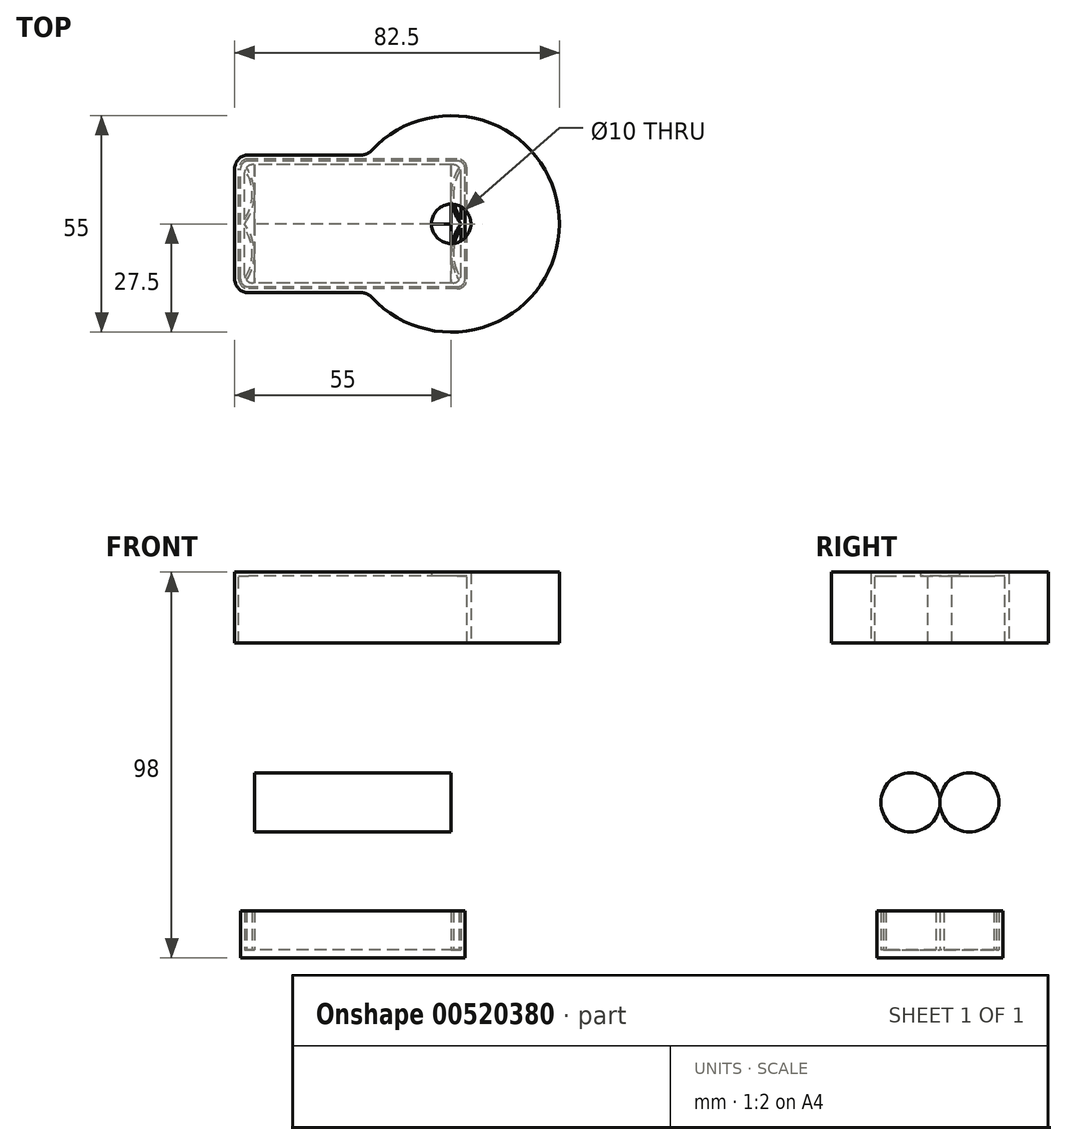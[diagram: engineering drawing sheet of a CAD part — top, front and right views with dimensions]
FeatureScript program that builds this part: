
annotation { "Feature Type Name" : "Feature", "Feature Type Description" : "" }
export const myFeature = defineFeature(function(context is Context, id is Id, definition is map)
    precondition{}
    {
        {
            var Q0;
            Q0=qCreatedBy(makeId("Top.planeOp"),FACE);
            var sketch = newSketch(context, id + "F0", { "sketchPlane" : qUnion([Q0])});
            skLineSegment(sketch, "E0.bottom", {"start": v(28.5, -16) * mm, "end": v(-28.5, -16) * mm});
            skLineSegment(sketch, "E0.top", {"start": v(28.5, 16) * mm, "end": v(-28.5, 16) * mm});
            skLineSegment(sketch, "E0.left", {"start": v(28.5, -16) * mm, "end": v(28.5, 16) * mm});
            skLineSegment(sketch, "E0.right", {"start": v(-28.5, -16) * mm, "end": v(-28.5, 16) * mm});
            skPoint(sketch, "E0.middle", {"position": v(0, 0) * mm});
            skLineSegment(sketch, "E1.bottom", {"start": v(27.5, -15) * mm, "end": v(-27.5, -15) * mm});
            skLineSegment(sketch, "E1.top", {"start": v(27.5, 15) * mm, "end": v(-27.5, 15) * mm});
            skLineSegment(sketch, "E1.left", {"start": v(27.5, -15) * mm, "end": v(27.5, 15) * mm});
            skLineSegment(sketch, "E1.right", {"start": v(-27.5, -15) * mm, "end": v(-27.5, 15) * mm});
            skSolve(sketch);
        }
        {
            var Q0;
            Q0=makeQuery(id+"F0.imprint","IMPRINT",FACE,{"disambiguationData":[TD([[makeQuery(id+"F0.imprint","IMPRINT",EDGE,{"derivedFrom":sQuery(id+"F0.wireOp",EDGE,"E0.bottom")}),-1.0]])]});
            var Q1;
            Q1=makeQuery(id+"F0.imprint","IMPRINT",FACE,{"disambiguationData":[TD([[makeQuery(id+"F0.imprint","IMPRINT",EDGE,{"derivedFrom":sQuery(id+"F0.wireOp",EDGE,"E1.bottom")}),-1.0]])]});
            extrude(context, id + "F1", {"entities" : qUnion([Q0, Q1]), "oppositeDirection" : true, "depth" : 2 * mm});
        }
        {
            var Q0;
            Q0=makeQuery(id+"F0.imprint","IMPRINT",FACE,{"disambiguationData":[TD([[makeQuery(id+"F0.imprint","IMPRINT",EDGE,{"derivedFrom":sQuery(id+"F0.wireOp",EDGE,"511JZqgd-saJz-wMDc-ROUc-2f22ZJkLcz4P.bottom")}),-1.0]])]});
            var Q1;
            {var subQ0=sQuery(id+"F0.wireOp",EDGE,"E0.bottom");Q1=makeQuery(id+"F0.imprint","IMPRINT",FACE,{"disambiguationData":[TD([[makeQuery(id+"F0.imprint","IMPRINT",EDGE,{"derivedFrom":subQ0}),-1.0]])]});}
            extrude(context, id + "F2", {"entities" : qUnion([Q0, Q1]), "operationType" : NewBodyOperationType.ADD, "depth" : 10 * mm});
        }
        {
            var Q0;
            Q0=makeQuery(id+"F2.opExtrude","SWEPT_EDGE",EDGE,{"disambiguationData":[OSD([sQuery(id+"F0.wireOp",EDGE,"E1.top"),sQuery(id+"F0.wireOp",EDGE,"E1.right")])]});
            var Q1;
            {var subQ0=sQuery(id+"F0.wireOp",EDGE,"E0.right");var subQ1=sQuery(id+"F0.wireOp",EDGE,"E0.top");Q1=makeQuery(id+"F2.boolean.opBoolean","MERGE",EDGE,{"derivedFrom":[makeQuery(id+"F1.opExtrude","SWEPT_EDGE",EDGE,{"disambiguationData":[OSD([subQ1,subQ0])]}),makeQuery(id+"F2.opExtrude","SWEPT_EDGE",EDGE,{"disambiguationData":[OSD([subQ1,subQ0])]})]});}
            var Q2;
            Q2=makeQuery(id+"F2.opExtrude","SWEPT_EDGE",EDGE,{"disambiguationData":[OSD([sQuery(id+"F0.wireOp",EDGE,"E1.bottom"),sQuery(id+"F0.wireOp",EDGE,"E1.right")])]});
            var Q3;
            {var subQ0=sQuery(id+"F0.wireOp",EDGE,"E0.left");var subQ1=sQuery(id+"F0.wireOp",EDGE,"E0.top");Q3=makeQuery(id+"F2.boolean.opBoolean","MERGE",EDGE,{"derivedFrom":[makeQuery(id+"F1.opExtrude","SWEPT_EDGE",EDGE,{"disambiguationData":[OSD([subQ1,subQ0])]}),makeQuery(id+"F2.opExtrude","SWEPT_EDGE",EDGE,{"disambiguationData":[OSD([subQ1,subQ0])]})]});}
            var Q4;
            {var subQ0=sQuery(id+"F0.wireOp",EDGE,"E0.right");var subQ1=sQuery(id+"F0.wireOp",EDGE,"E0.bottom");Q4=makeQuery(id+"F2.boolean.opBoolean","MERGE",EDGE,{"derivedFrom":[makeQuery(id+"F1.opExtrude","SWEPT_EDGE",EDGE,{"disambiguationData":[OSD([subQ1,subQ0])]}),makeQuery(id+"F2.opExtrude","SWEPT_EDGE",EDGE,{"disambiguationData":[OSD([subQ1,subQ0])]})]});}
            var Q5;
            Q5=makeQuery(id+"F2.opExtrude","SWEPT_EDGE",EDGE,{"disambiguationData":[OSD([sQuery(id+"F0.wireOp",EDGE,"E1.top"),sQuery(id+"F0.wireOp",EDGE,"E1.left")])]});
            var Q6;
            Q6=makeQuery(id+"F2.opExtrude","SWEPT_EDGE",EDGE,{"disambiguationData":[OSD([sQuery(id+"F0.wireOp",EDGE,"E1.bottom"),sQuery(id+"F0.wireOp",EDGE,"E1.left")])]});
            var Q7;
            {var subQ0=sQuery(id+"F0.wireOp",EDGE,"E0.left");var subQ1=sQuery(id+"F0.wireOp",EDGE,"E0.bottom");Q7=makeQuery(id+"F2.boolean.opBoolean","MERGE",EDGE,{"derivedFrom":[makeQuery(id+"F1.opExtrude","SWEPT_EDGE",EDGE,{"disambiguationData":[OSD([subQ1,subQ0])]}),makeQuery(id+"F2.opExtrude","SWEPT_EDGE",EDGE,{"disambiguationData":[OSD([subQ1,subQ0])]})]});}
            var Q8;
            Q8=makeQuery(id+"F2.opExtrude","CAP_EDGE",EDGE,{"disambiguationData":[OSD([sQuery(id+"F0.wireOp",EDGE,"E1.top")])],"isStart":true});
            var Q9;
            Q9=makeQuery(id+"F2.opExtrude","CAP_EDGE",EDGE,{"disambiguationData":[OSD([sQuery(id+"F0.wireOp",EDGE,"E1.bottom")])],"isStart":true});
            fillet(context, id + "F3", {"entities" : qUnion([Q0, Q1, Q2, Q3, Q4, Q5, Q6, Q7, Q8, Q9]), "radius" : 2 * mm, "tangentPropagation" : true, "allowEdgeOverflow" : false});
        }
        {
            var Q0;
            Q0=qCreatedBy(makeId("Right.planeOp"),FACE);
            var sketch = newSketch(context, id + "F4", { "sketchPlane" : qUnion([Q0])});
            skCircle(sketch, "E2", {"center": v(-7.5, 7.5) * mm, "radius": 7.5 * mm});
            skCircle(sketch, "E3.MirrorC", {"center": v(7.5, 7.5) * mm, "radius": 7.5 * mm});
            skSolve(sketch);
        }
        {
            var Q0;
            Q0=qSketchRegion(id+"F4",true);
            extrude(context, id + "F5", {"entities" : qUnion([Q0]), "endBound" : BoundingType.SYMMETRIC, "depth" : 50 * mm});
        }
        {
            var Q0;
            Q0=qCreatedBy(makeId("Top.planeOp"),FACE);
            var sketch = newSketch(context, id + "F6", { "sketchPlane" : qUnion([Q0])});
            skLineSegment(sketch, "E4.0", {"start": v(-27.5, -15) * mm, "end": v(-27.5, 15) * mm, "construction": true});
            skLineSegment(sketch, "E5.0", {"start": v(-25, 0) * mm, "end": v(-25, 15) * mm, "construction": true});
            skArc(sketch, "E6", {"start": v(-27.5, 0) * mm, "mid": v(-25, 7.5) * mm, "end": v(-27.5, 15) * mm});
            skArc(sketch, "E7", {"start": v(-27.5, 1.05) * mm, "mid": v(-25.6, 7.5) * mm, "end": v(-27.5, 13.95) * mm});
            skLineSegment(sketch, "E8", {"start": v(-27.5, 15) * mm, "end": v(-27.5, 13.95) * mm});
            skLineSegment(sketch, "E9", {"start": v(-27.5, 1.05) * mm, "end": v(-27.5, 0) * mm});
            skLineSegment(sketch, "E10.MirrorCS", {"start": v(-27.5, -15) * mm, "end": v(-27.5, -13.95) * mm});
            skArc(sketch, "E11.MirrorCS", {"start": v(-27.5, -1.05) * mm, "mid": v(-25.6, -7.5) * mm, "end": v(-27.5, -13.95) * mm});
            skArc(sketch, "E12.MirrorCS", {"start": v(-27.5, 0) * mm, "mid": v(-25, -7.5) * mm, "end": v(-27.5, -15) * mm});
            skLineSegment(sketch, "E13.MirrorCS", {"start": v(-27.5, -1.05) * mm, "end": v(-27.5, 0) * mm});
            skLineSegment(sketch, "E14.MirrorCS", {"start": v(-25, 0) * mm, "end": v(-25, -15) * mm, "construction": true});
            skLineSegment(sketch, "E15.MirrorCS", {"start": v(27.5, -1.05) * mm, "end": v(27.5, 0) * mm});
            skLineSegment(sketch, "E16.MirrorCS", {"start": v(27.5, -15) * mm, "end": v(27.5, -13.95) * mm});
            skLineSegment(sketch, "E17.MirrorCS", {"start": v(27.5, 15) * mm, "end": v(27.5, 13.95) * mm});
            skLineSegment(sketch, "E18.MirrorCS", {"start": v(27.5, 1.05) * mm, "end": v(27.5, 0) * mm});
            skLineSegment(sketch, "E19.MirrorCS", {"start": v(27.5, -15) * mm, "end": v(27.5, 15) * mm, "construction": true});
            skLineSegment(sketch, "E20.MirrorCS", {"start": v(25, 0) * mm, "end": v(25, -15) * mm, "construction": true});
            skArc(sketch, "E21.MirrorCS", {"start": v(27.5, 0) * mm, "mid": v(25, -7.5) * mm, "end": v(27.5, -15) * mm});
            skArc(sketch, "E22.MirrorCS", {"start": v(27.5, 0) * mm, "mid": v(25, 7.5) * mm, "end": v(27.5, 15) * mm});
            skLineSegment(sketch, "E23.MirrorCS", {"start": v(25, 0) * mm, "end": v(25, 15) * mm, "construction": true});
            skArc(sketch, "E24.MirrorCS", {"start": v(27.5, 1.05) * mm, "mid": v(25.6, 7.5) * mm, "end": v(27.5, 13.95) * mm});
            skArc(sketch, "E25.MirrorCS", {"start": v(27.5, -1.05) * mm, "mid": v(25.6, -7.5) * mm, "end": v(27.5, -13.95) * mm});
            skSolve(sketch);
        }
        {
            var Q0;
            Q0=makeQuery(id+"F6.imprint","IMPRINT",FACE,{"disambiguationData":[TD([[makeQuery(id+"F6.imprint","IMPRINT",EDGE,{"derivedFrom":sQuery(id+"F6.wireOp",EDGE,"E6")}),1.0]])]});
            var Q1;
            Q1=makeQuery(id+"F6.imprint","IMPRINT",FACE,{"disambiguationData":[TD([[makeQuery(id+"F6.imprint","IMPRINT",EDGE,{"derivedFrom":sQuery(id+"F6.wireOp",EDGE,"E10.MirrorCS")}),-1.0]])]});
            var Q2;
            Q2=makeQuery(id+"F6.imprint","IMPRINT",FACE,{"disambiguationData":[TD([[makeQuery(id+"F6.imprint","IMPRINT",EDGE,{"derivedFrom":sQuery(id+"F6.wireOp",EDGE,"E17.MirrorCS")}),-1.0]])]});
            var Q3;
            Q3=makeQuery(id+"F6.imprint","IMPRINT",FACE,{"disambiguationData":[TD([[makeQuery(id+"F6.imprint","IMPRINT",EDGE,{"derivedFrom":sQuery(id+"F6.wireOp",EDGE,"E15.MirrorCS")}),1.0]])]});
            extrude(context, id + "F7", {"entities" : qUnion([Q0, Q1, Q2, Q3]), "operationType" : NewBodyOperationType.ADD, "depth" : 10 * mm});
        }
        {
            var Q0;
            Q0=qCreatedBy(makeId("Top.planeOp"),FACE);
            cPlane(context, id + "F8", {"entities" : qUnion([Q0]), "cplaneType" : CPlaneType.OFFSET, "offset" : 15 * mm, "width" : 150 * mm, "height" : 150 * mm});
        }
        {
            var Q0;
            Q0=qCreatedBy(id+"F8.planeOp",FACE);
            var sketch = newSketch(context, id + "F9", { "sketchPlane" : qUnion([Q0])});
            skLineSegment(sketch, "E26.bottom", {"start": v(26.5, -16.5) * mm, "end": v(-26.5, -16.5) * mm});
            skLineSegment(sketch, "E26.top", {"start": v(26.5, 16.5) * mm, "end": v(-26.5, 16.5) * mm});
            skLineSegment(sketch, "E26.left", {"start": v(29, -14) * mm, "end": v(29, 14) * mm});
            skLineSegment(sketch, "E26.right", {"start": v(-29, -14) * mm, "end": v(-29, 14) * mm});
            skPoint(sketch, "E26.middle", {"position": v(0, 0) * mm});
            skPoint(sketch, "E27.visualSharp", {"position": v(-29, 16.5) * mm});
            skArc(sketch, "E27.filletArc", {"start": v(-26.5, 16.5) * mm, "mid": v(-28.27, 15.77) * mm, "end": v(-29, 14) * mm});
            skPoint(sketch, "E28.visualSharp", {"position": v(29, 16.5) * mm});
            skArc(sketch, "E28.filletArc", {"start": v(29, 14) * mm, "mid": v(28.27, 15.77) * mm, "end": v(26.5, 16.5) * mm});
            skPoint(sketch, "E29.visualSharp", {"position": v(29, -16.5) * mm});
            skArc(sketch, "E29.filletArc", {"start": v(26.5, -16.5) * mm, "mid": v(28.27, -15.77) * mm, "end": v(29, -14) * mm});
            skPoint(sketch, "E30.visualSharp", {"position": v(-29, -16.5) * mm});
            skArc(sketch, "E30.filletArc", {"start": v(-29, -14) * mm, "mid": v(-28.27, -15.77) * mm, "end": v(-26.5, -16.5) * mm});
            skLineSegment(sketch, "E31.bottom", {"start": v(2.2, -17.5) * mm, "end": v(-26.5, -17.5) * mm});
            skLineSegment(sketch, "E31.top", {"start": v(2.2, 17.5) * mm, "end": v(-26.5, 17.5) * mm});
            skLineSegment(sketch, "E31.left", {"start": v(30, -27.04) * mm, "end": v(30, 27.04) * mm});
            skLineSegment(sketch, "E31.right", {"start": v(-30, -14) * mm, "end": v(-30, 14) * mm});
            skPoint(sketch, "E32.visualSharp", {"position": v(-30, 17.5) * mm});
            skArc(sketch, "E32.filletArc", {"start": v(-26.5, 17.5) * mm, "mid": v(-28.97, 16.47) * mm, "end": v(-30, 14) * mm});
            skPoint(sketch, "E33.visualSharp", {"position": v(-30, -17.5) * mm});
            skArc(sketch, "E33.filletArc", {"start": v(-30, -14) * mm, "mid": v(-28.97, -16.47) * mm, "end": v(-26.5, -17.5) * mm});
            skArc(sketch, "E34", {"start": v(4.77, -18.63) * mm, "mid": v(52.5, 0) * mm, "end": v(4.77, 18.63) * mm});
            skPoint(sketch, "E35.orphan", {"position": v(30, 17.5) * mm});
            skPoint(sketch, "E36.orphan", {"position": v(30, -17.5) * mm});
            skCircle(sketch, "E37", {"center": v(25, 0) * mm, "radius": 5 * mm});
            skPoint(sketch, "E38.visualSharp", {"position": v(3.79, 17.5) * mm});
            skArc(sketch, "E38.filletArc", {"start": v(2.2, 17.5) * mm, "mid": v(3.6, 17.8) * mm, "end": v(4.77, 18.63) * mm});
            skPoint(sketch, "E39.visualSharp", {"position": v(3.79, -17.5) * mm});
            skArc(sketch, "E39.filletArc", {"start": v(4.77, -18.63) * mm, "mid": v(3.6, -17.8) * mm, "end": v(2.2, -17.5) * mm});
            skSolve(sketch);
        }
        {
            var Q0;
            Q0=makeQuery(id+"F9.imprint","IMPRINT",FACE,{"disambiguationData":[TD([[makeQuery(id+"F9.imprint","IMPRINT",EDGE,{"derivedFrom":sQuery(id+"F9.wireOp",EDGE,"E26.bottom")}),-1.0]])]});
            var Q1;
            Q1=makeQuery(id+"F9.imprint","IMPRINT",FACE,{"disambiguationData":[TD([[makeQuery(id+"F9.imprint","IMPRINT",EDGE,{"derivedFrom":sQuery(id+"F9.wireOp",EDGE,"E26.bottom")}),1.0]])]});
            var Q2;
            {var subQ0=sQuery(id+"F9.wireOp",EDGE,"E34");var subQ1=sQuery(id+"F9.wireOp",EDGE,"E31.left");var subQ2=makeQuery(id+"F9.imprint","INTERSECT",VERTEX,{"disambiguationData":[OD(0.0)],"derivedFrom":[subQ1,subQ0]});Q2=makeQuery(id+"F9.imprint","IMPRINT",FACE,{"disambiguationData":[TD([[makeQuery(id+"F9.imprint","IMPRINT",EDGE,{"disambiguationData":[TD([[subQ2,-1.0]])],"derivedFrom":subQ1}),-1.0]])]});}
            extrude(context, id + "F10", {"entities" : qUnion([Q0, Q1, Q2]), "depth" : 1 * mm});
        }
        {
            var Q0;
            Q0=qSketchRegion(id+"F9",true);
            var Q1;
            {var subQ0=sQuery(id+"F9.wireOp",EDGE,"E37");var subQ1=sQuery(id+"F9.wireOp",EDGE,"E26.left");var subQ2=makeQuery(id+"F9.imprint","INTERSECT",VERTEX,{"disambiguationData":[OD(0.0)],"derivedFrom":[subQ1,subQ0]});Q1=makeQuery(id+"F9.imprint","IMPRINT",FACE,{"disambiguationData":[TD([[makeQuery(id+"F9.imprint","IMPRINT",EDGE,{"disambiguationData":[TD([[subQ2,-1.0]])],"derivedFrom":subQ1}),-1.0]])]});}
            extrude(context, id + "F11", {"entities" : qUnion([Q0, Q1]), "operationType" : NewBodyOperationType.ADD, "oppositeDirection" : true, "depth" : 17 * mm});
        }
        {
            var Q0;
            Q0=makeQuery(id+"F10.opExtrude","SWEPT_BODY",BODY,{"disambiguationData":[OSD([sQuery(id+"F9.wireOp",EDGE,"E31.bottom"),sQuery(id+"F9.wireOp",EDGE,"E31.top"),sQuery(id+"F9.wireOp",EDGE,"E31.right"),sQuery(id+"F9.wireOp",EDGE,"E32.filletArc"),sQuery(id+"F9.wireOp",EDGE,"E33.filletArc"),sQuery(id+"F9.wireOp",EDGE,"E34"),sQuery(id+"F9.wireOp",EDGE,"E37"),sQuery(id+"F9.wireOp",EDGE,"E38.filletArc"),sQuery(id+"F9.wireOp",EDGE,"E39.filletArc")])]});
            transform(context, id + "F12", {"entities" : qUnion([Q0]), "transformType" : TransformType.TRANSLATION_3D, "dx" : 0 * mm, "dy" : 0 * mm, "dz" : 50 * mm, "makeCopy" : false});
        }
        {
            var Q0;
            Q0=makeQuery(id+"F1.opExtrude","SWEPT_BODY",BODY,{"disambiguationData":[OSD([sQuery(id+"F0.wireOp",EDGE,"E0.bottom"),sQuery(id+"F0.wireOp",EDGE,"E0.top"),sQuery(id+"F0.wireOp",EDGE,"E0.left"),sQuery(id+"F0.wireOp",EDGE,"E0.right")])]});
            transform(context, id + "F13", {"entities" : qUnion([Q0]), "transformType" : TransformType.TRANSLATION_3D, "dx" : 0 * mm, "dy" : 0 * mm, "dz" : -30 * mm, "makeCopy" : false});
        }
    });
